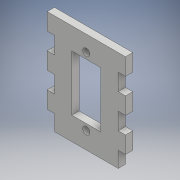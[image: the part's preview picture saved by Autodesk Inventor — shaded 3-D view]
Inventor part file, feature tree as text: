
AUTODESK INVENTOR PART (.ipt)
format: ipt  version: 2018 (Build 220112000, 112)  size: 164,864 bytes
history: native  units: mm
features: extrude x5, sketch x5, other x1
ambient origin geometry x8: Origin, YZ Plane, XZ Plane, XY Plane, X Axis, Y Axis, Z Axis, Center Point
bodies: Body1 (feature_tree)
feature tree (11):
  other  "Sólido1"
  extrude  "Extrusión1"  Depth=7.0mm
  extrude  "Extrusión2"  Depth=3.0mm TaperAngle=0.0deg
  extrude  "Extrusión3"  Depth=3.0mm TaperAngle=0.0deg
  extrude  "Extrusión4"  [1 undecoded]
  extrude  "Extrusión5"  [1 undecoded]
  sketch  "Boceto1"  dims[d4=3.0mm d5=0.0mm d19=7.0mm]
  sketch  "Boceto2"  dims[d20=3.0mm d21=3.0mm d22=0.0mm]
  sketch  "Boceto3"  dims[d29=3.0mm d30=0.0mm d32=3.0mm d33=0.0mm]
  sketch  "Boceto4"  dims[d34=3.0mm d35=0.0mm]
  sketch  "Boceto5"
note: 2 required parameter values undecoded (feature->parameter linkage not recoverable at this tier; creation-order binding heuristic only, values carry confidence <= 0.55)
